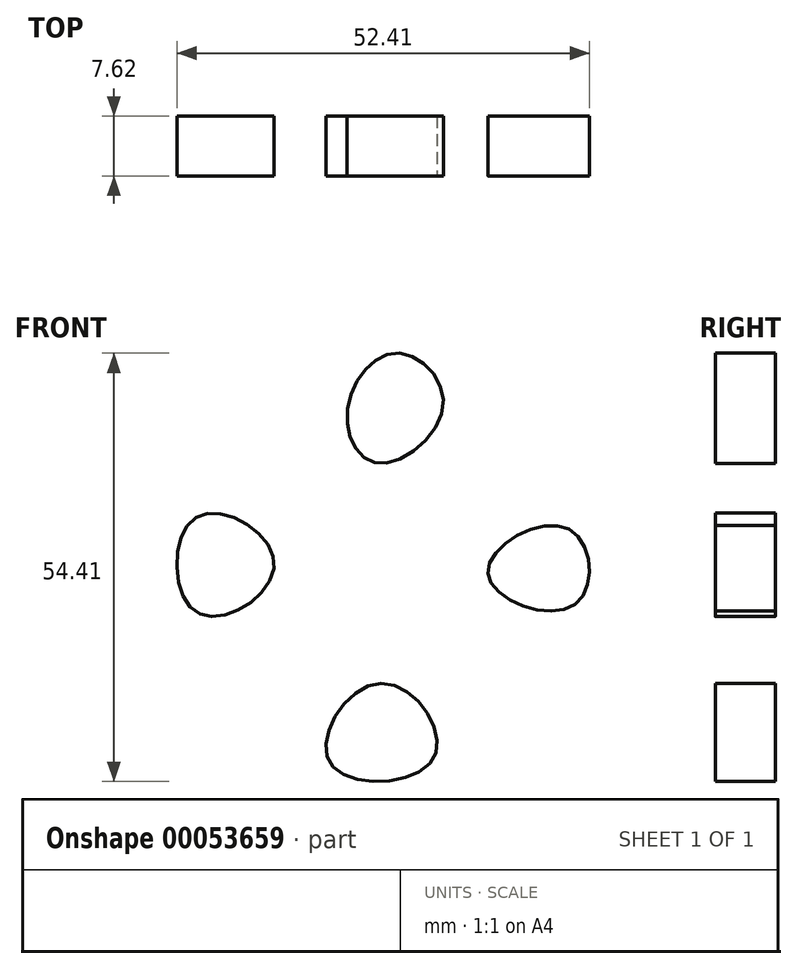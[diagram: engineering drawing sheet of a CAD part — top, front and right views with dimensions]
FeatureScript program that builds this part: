
annotation { "Feature Type Name" : "Feature", "Feature Type Description" : "" }
export const myFeature = defineFeature(function(context is Context, id is Id, definition is map)
    precondition{}
    {
        {
            var Q0;
            Q0=qCreatedBy(makeId("Front.planeOp"),FACE);
            var sketch = newSketch(context, id + "F0", { "sketchPlane" : qUnion([Q0])});
            skCircle(sketch, "E0", {"center": v(-41.32, 37.07) * mm, "radius": 33.23 * mm});
            skSolve(sketch);
        }
        {
            var Q0;
            Q0=makeQuery(id+"F0.imprint","IMPRINT",FACE,{"disambiguationData":[TD([[makeQuery(id+"F0.imprint","IMPRINT",EDGE,{"derivedFrom":sQuery(id+"F0.wireOp",EDGE,"E0")}),1.0]])]});
            var sketch = newSketch(context, id + "F1", { "sketchPlane" : qUnion([Q0])});
            skCircle(sketch, "E1", {"center": v(-41.52, 37.07) * mm, "radius": 11.35 * mm});
            skCircle(sketch, "E2", {"center": v(-41.73, 43.35) * mm, "radius": 2.03 * mm});
            skCircle(sketch, "E3", {"center": v(-33.42, 36.46) * mm, "radius": 2.24 * mm});
            skCircle(sketch, "E4", {"center": v(-41.52, 29.37) * mm, "radius": 1.87 * mm});
            skCircle(sketch, "E5", {"center": v(-48.82, 36.87) * mm, "radius": 2.24 * mm});
            skCircle(sketch, "E6", {"center": v(-41.52, 37.07) * mm, "radius": 1.83 * mm});
            skSolve(sketch);
        }
        {
            var Q0;
            Q0=makeQuery(id+"F0.imprint","IMPRINT",FACE,{"disambiguationData":[TD([[makeQuery(id+"F0.imprint","IMPRINT",EDGE,{"derivedFrom":sQuery(id+"F0.wireOp",EDGE,"E0")}),1.0]])]});
            var sketch = newSketch(context, id + "F2", { "sketchPlane" : qUnion([Q0])});
            skFitSpline(sketch, "E7", {"points": [v(-40.87, 23.7) * mm, v(-47.35, 13.57) * mm, v(-34.19, 14.18) * mm, v(-40.87, 23.7) * mm]});
            skFitSpline(sketch, "E8", {"points": [v(-27.3, 37.68) * mm, v(-17.17, 43.35) * mm, v(-16.36, 33.62) * mm, v(-27.3, 37.68) * mm]});
            skFitSpline(sketch, "E9", {"points": [v(-45.12, 58.54) * mm, v(-41.27, 51.65) * mm, v(-32.97, 58.94) * mm, v(-38.84, 65.63) * mm, v(-45.12, 58.54) * mm]});
            skFitSpline(sketch, "E10", {"points": [v(-64.37, 44.77) * mm, v(-54.44, 38.9) * mm, v(-64.16, 32.61) * mm, v(-64.37, 44.77) * mm]});
            skSolve(sketch);
        }
        {
            var Q0;
            Q0=sQuery(id+"F2.wireOp",EDGE,"E9");
            var Q1;
            Q1=sQuery(id+"F2.wireOp",EDGE,"E10");
            var Q2;
            Q2=sQuery(id+"F2.wireOp",EDGE,"E7");
            var Q3;
            Q3=sQuery(id+"F2.wireOp",EDGE,"E8");
            extrude(context, id + "F3", {"bodyType" : ToolBodyType.SURFACE, "surfaceEntities" : qUnion([Q0, Q1, Q2, Q3]), "depth" : 7.62 * mm});
        }
    });
